# Revit family: PRD_FrankeWS_SlbUrnls_CAMPUSSlabUrinalConnector_ZCMPX0002
name_source: partatom
category: Plumbing Fixtures
revit_build: Autodesk Revit 2018 (Build: 20190510_1515(x64)
units: mm (PartAtom-declared; Revit-internal decimal feet)

## family parameters
Always vertical = Yes
Cut with Voids When Loaded = No
OmniClass Number = 23.45.05.14.99
OmniClass Title = Other Sanitary Washing Plumbing Fixtures
Part Type = Normal
Room Calculation Point = No
Round Connector Dimension = Use Diameter
Shared = Yes
Work Plane-Based = No

## types (1)
- ZCMPX0002
    AssetType = Fixed
    BIMObjectName = PRD_AR_SlabUrinals_ConnectionPlateForTroughUrinal_ZCMPX0002
    Category = Pr_40_20_93_77, Slab urinals
    ConnectionPlateMaterial = PRD_AR_StainlessSteel_SatinFinished
    Description = Connector for urinal slabs CMPX551GE until CMPX555GE made of stainless steel, surface satin finished, material thickness 1 mm. For covering the joint of urinal slab combinations.
    DurationUnit = year
    Features = stainless steel, surface satin finished, material thickness 1 mm
    Finish = Satin finished
    GrossWeight = 2.00 kg
    IfcExportAs = IfcSanitaryTerminalType
    IfcExportType = URINAL
    Manufacturer = KWC Group AG
    ManufacturerName = KWC Group AG
    ManufacturerURL = www.kwc.com
    Material = Stainless steel
    Model = ZCMPX0002
    ModelNumber = 2030020577
    ModelReference = ZCMPX0002
    Mounting = Other
    NBSDescription = Urinal assembly
    NBSReference = 45-35-70/352
    Name = CAMPUS Slab urinal connector ZCMPX0002
    NetWeight = 0.19 kg
    NominalDepth = 0 mm  [stored 0 ft]
    NominalHeight = 365 mm
    NominalWidth = 37 mm
    ProductCode = 205.0638.902
    ProductInformation = https://pim.kwc.com
    Quantity = 1
    QuantityUom = Piece
    SpilloverLevel = 0 mm  [stored 0 ft]
    TailorMade = No
    URL = www.kwc.com
    Uniclass2015Code = Pr_40_20_93_77
    Uniclass2015Title = Slab urinals
    Uniclass2015Version = Products v1.23
    UrinalType = Trough
    Version = 1
    WarrantyDurationUnit = year

note: [stored X ft] marks values corroborated as IEEE doubles in the binary element streams (Revit-internal decimal feet)

## geometry (parser evidence)
native form markers: Sweep x2
no freeform markers — native parametric forms only
